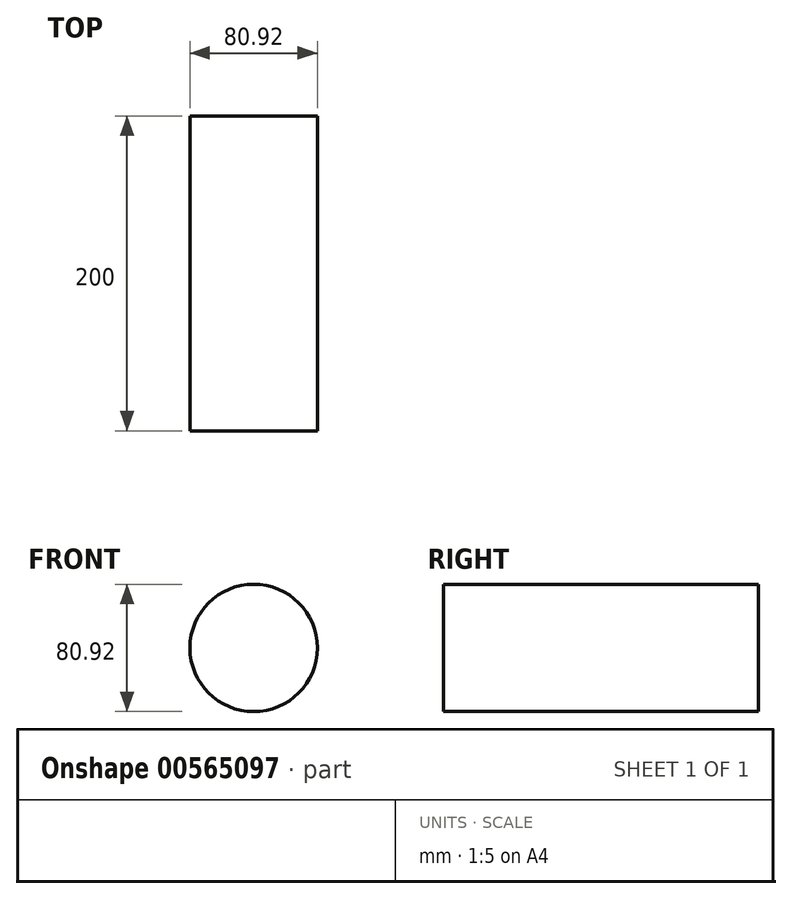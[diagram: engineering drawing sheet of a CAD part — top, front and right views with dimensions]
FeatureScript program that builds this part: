
annotation { "Feature Type Name" : "Feature", "Feature Type Description" : "" }
export const myFeature = defineFeature(function(context is Context, id is Id, definition is map)
    precondition{}
    {
        {
            var Q0;
            Q0=qCreatedBy(makeId("Front.planeOp"),FACE);
            var sketch = newSketch(context, id + "F0", { "sketchPlane" : qUnion([Q0])});
            skCircle(sketch, "E0", {"center": v(0, 0) * mm, "radius": 40.46 * mm});
            skSolve(sketch);
        }
        {
            var Q0;
            Q0 = qSketchRegion(id + "F0", true);
            extrude(context, id + "F1", {"entities" : qUnion([Q0]), "depth" : 200 * mm, "offsetDistance" : 25 * mm});
        }
    });
